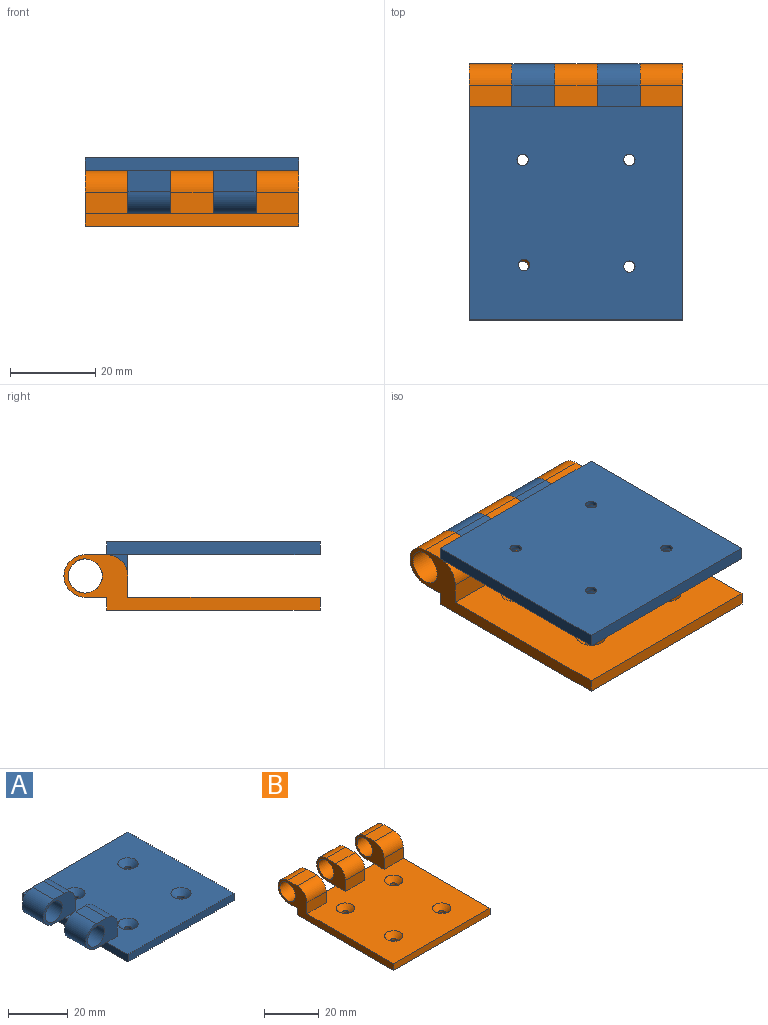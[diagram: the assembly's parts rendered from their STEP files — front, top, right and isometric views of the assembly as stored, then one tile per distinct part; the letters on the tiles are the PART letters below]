
ASSEMBLY  parts=2 mates=1
PART A: 30 faces, bbox 60x50x13 mm
  f0: plane 50x3mm, normal (-1,0,0), area 150mm2, adj f5,f11,f12,f13,f20,f21
  f1: plane 10x5mm, normal (1,0,0), area 50mm2, adj f3,f7,f8,f20
  f2: plane 10x5mm, normal (1,0,0), area 50mm2, adj f4,f15,f16,f20
  f3: cylinder r=5mm len=10mm, axis (0,-1,0), area 78.5mm2, adj f1,f6,f7,f8
  f4: cylinder r=5mm len=10mm, axis (0,-1,0), area 78.5mm2, adj f2,f14,f15,f16
  f5: plane 10x5mm, normal (0,0,-1), area 50mm2, adj f0,f7,f8,f9
  f6: plane 10x5mm, normal (0,0,1), area 50mm2, adj f3,f7,f8,f9
  f7: plane 15x10mm, normal (0,-1,0), area 83.6mm2, adj f1,f3,f5,f6,f9,f10,f20
  f8: plane 15x10mm, normal (0,1,0), area 83.6mm2, adj f1,f3,f5,f6,f9,f10,f20
  f9: cylinder r=5mm len=10mm, axis (0,-1,0), area 157.1mm2, adj f5,f6,f7,f8
  f10: cylinder r=4mm len=10mm, axis (0,1,0), area 251.3mm2, adj f7,f8
  f11: plane 50x3mm, normal (0,1,0), area 150mm2, adj f0,f19,f20,f21
  f12: plane 50x3mm, normal (0,-1,0), area 150mm2, adj f0,f19,f20,f21
  f13: plane 10x5mm, normal (0,0,-1), area 50mm2, adj f0,f15,f16,f17
  f14: plane 10x5mm, normal (0,0,1), area 50mm2, adj f4,f15,f16,f17
  f15: plane 15x10mm, normal (0,1,0), area 83.6mm2, adj f2,f4,f13,f14,f17,f18,f20
  f16: plane 15x10mm, normal (0,-1,0), area 83.6mm2, adj f2,f4,f13,f14,f17,f18,f20
  f17: cylinder r=5mm len=10mm, axis (0,-1,0), area 157.1mm2, adj f13,f14,f15,f16
  f18: cylinder r=4mm len=10mm, axis (0,1,0), area 251.3mm2, adj f15,f16
  f19: plane 50x3mm, normal (1,0,0), area 150mm2, adj f11,f12,f20,f21
  f20: plane 50x50mm, normal (0,0,1), area 2258.1mm2, adj f0,f1,f2,f7,f8,f11,f12,f15
  f21: plane 50x50mm, normal (0,0,-1), area 2477.9mm2, adj f0,f11,f12,f19,f22,f24,f26,f28
  f22: cylinder r=1.32mm len=2.65mm, axis (0,0,1), area 8mm2, adj f21,f23
  f23: cone r=1.32mm half-angle=45deg, axis (0,0,1), area 42.4mm2, adj f20,f22
  f24: cylinder r=1.32mm len=2.65mm, axis (0,0,1), area 8mm2, adj f21,f25
  f25: cone r=1.32mm half-angle=45deg, axis (0,0,1), area 42.4mm2, adj f20,f24
  f26: cylinder r=1.32mm len=2.65mm, axis (0,0,1), area 8mm2, adj f21,f27
  f27: cone r=1.32mm half-angle=45deg, axis (0,0,1), area 42.4mm2, adj f20,f26
  f28: cylinder r=1.32mm len=2.65mm, axis (0,0,1), area 8mm2, adj f21,f29
  f29: cone r=1.32mm half-angle=45deg, axis (0,0,1), area 42.4mm2, adj f20,f28
PART B: 36 faces, bbox 50x60x13 mm
  f0: plane 10x5mm, normal (0,-1,0), area 50mm2, adj f2,f6,f8,f20
  f1: plane 10x5mm, normal (0,-1,0), area 50mm2, adj f3,f16,f17,f20
  f2: cylinder r=5mm len=10mm, axis (-1,0,0), area 78.5mm2, adj f0,f5,f6,f8
  f3: cylinder r=5mm len=10mm, axis (-1,0,0), area 78.5mm2, adj f1,f16,f17,f18
  f4: plane 10x5mm, normal (0,0,-1), area 50mm2, adj f6,f8,f9,f10
  f5: plane 10x5mm, normal (0,0,1), area 50mm2, adj f2,f6,f8,f9
  f6: plane 60x13mm, normal (1,0,0), area 233.6mm2, adj f0,f2,f4,f5,f7,f9,f10,f20
  f7: cylinder r=4mm len=10mm, axis (1,0,0), area 251.3mm2, adj f6,f8
  f8: plane 15x10mm, normal (-1,0,0), area 83.6mm2, adj f0,f2,f4,f5,f7,f9,f20
  f9: cylinder r=5mm len=10mm, axis (1,0,0), area 157.1mm2, adj f4,f5,f6,f8
  f10: plane 50x3mm, normal (0,1,0), area 150mm2, adj f4,f6,f11,f12,f20,f22,f32
  f11: plane 10x5mm, normal (0,0,-1), area 50mm2, adj f10,f16,f17,f19
  f12: plane 60x13mm, normal (-1,0,0), area 233.6mm2, adj f10,f13,f14,f20,f21,f22,f31,f32
  f13: plane 10x5mm, normal (0,-1,0), area 50mm2, adj f12,f14,f20,f34
  f14: cylinder r=5mm len=10mm, axis (-1,0,0), area 78.5mm2, adj f12,f13,f31,f34
  f15: cylinder r=4mm len=10mm, axis (1,0,0), area 251.3mm2, adj f16,f17
  f16: plane 15x10mm, normal (1,0,0), area 83.6mm2, adj f1,f3,f11,f15,f18,f19,f20
  f17: plane 15x10mm, normal (-1,0,0), area 83.6mm2, adj f1,f3,f11,f15,f18,f19,f20
  f18: plane 10x5mm, normal (0,0,1), area 50mm2, adj f3,f16,f17,f19
  f19: cylinder r=5mm len=10mm, axis (1,0,0), area 157.1mm2, adj f11,f16,f17,f18
  f20: plane 50x50mm, normal (0,0,1), area 2208.1mm2, adj f0,f1,f6,f8,f10,f12,f13,f16
  f21: plane 50x3mm, normal (0,-1,0), area 150mm2, adj f6,f12,f20,f22
  f22: plane 50x50mm, normal (0,0,-1), area 2477.9mm2, adj f6,f10,f12,f21,f23,f25,f27,f29
  f23: cylinder r=1.32mm len=2.65mm, axis (0,0,1), area 8mm2, adj f22,f24
  f24: cone r=1.32mm half-angle=45deg, axis (0,0,1), area 42.4mm2, adj f20,f23
  f25: cylinder r=1.32mm len=2.65mm, axis (0,0,1), area 8mm2, adj f22,f26
  f26: cone r=1.32mm half-angle=45deg, axis (0,0,1), area 42.4mm2, adj f20,f25
  f27: cylinder r=1.32mm len=2.65mm, axis (0,0,1), area 8mm2, adj f22,f28
  f28: cone r=1.32mm half-angle=45deg, axis (0,0,1), area 42.4mm2, adj f20,f27
  f29: cylinder r=1.32mm len=2.65mm, axis (0,0,1), area 8mm2, adj f22,f30
  f30: cone r=1.32mm half-angle=45deg, axis (0,0,1), area 42.4mm2, adj f20,f29
  f31: plane 10x5mm, normal (0,0,1), area 50mm2, adj f12,f14,f34,f35
  f32: plane 10x5mm, normal (0,0,-1), area 50mm2, adj f10,f12,f34,f35
  f33: cylinder r=4mm len=10mm, axis (1,0,0), area 251.3mm2, adj f12,f34
  f34: plane 15x10mm, normal (1,0,0), area 83.6mm2, adj f13,f14,f20,f31,f32,f33,f35
  f35: cylinder r=5mm len=10mm, axis (1,0,0), area 157.1mm2, adj f12,f31,f32,f34
PLACE A rot(axis=(0.71,-0.71,0),180deg) t=(0,0,16)mm
PLACE B at identity
MATE revolute A.f10 <-> B.f7  axis (1,0,0) through (-5,30,8)mm
